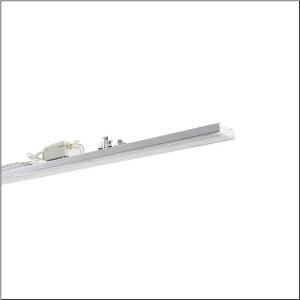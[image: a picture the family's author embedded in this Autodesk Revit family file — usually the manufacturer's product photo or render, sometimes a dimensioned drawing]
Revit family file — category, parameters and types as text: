
# Revit family: licross_r__11_recessed_mo_51te19mn495g_12e7
name_source: partatom
category: Lighting Fixtures
units: mm (PartAtom-declared; Revit-internal decimal feet)

## family parameters
Cut with Voids When Loaded = No
Host = Face
Light Source = No
Part Type = Normal
Room Calculation Point = No
Round Connector Dimension = Use Diameter
Shared = No

## types (1)
- --- (1 x LED, 9850 lm, 55.2 W, 4000K)
    Apparent Load = 55 VA
    CIE Flux Codes = 55 90 98 100 100
    Color Rendering = 80
    Color Temperature = 4000K
    Default Elevation = 1800 mm
    Description = Licross® 11 Recessed MO, luminaire insert, of sheet steel, galvanised, coil coated, white, length: 1.500mm, width: 66mm, height: 67mm, LED rated luminous flux: 9.860lm, light colour: 840, control gear: ON/OFF Multilumen, with plug, 3-pole, with phase selection, mains connection: 220..240V, AC, 50/60Hz, rated input power: 55W, halogen-free wiring, primary light control with lens, of plastic, primary optical cover: cover, of PMMA, light emission: direct distribution, primary light characteristic: double asymmetric, protection rating (complete): IP54, insulation class (complete): insulation class I (protective earthing), certification: CE, ENEC, VDE, UKCA, protection symbol: D if used in an environment with non-conductive dust loads with corresponding accessories, impact resistance: IK06, permissible ambient temperature for indoor applications: -35..+40°C, corresponds to IFS (International Featured Standards) requirements for safety and quality in the food industry, reducing of maximum allowable ambient temperature of 5°C with ceiling mounting, packaging unit: 1 piece
    Height = 58 mm
    Lamp = 1 x LED
    Lamp Light Flux = 9850 lm
    Lamp Power = 55.2 W
    Lamp count = 1
    Length = 1500 mm
    Luminous efficacy = 178 lm/W
    Manufacturer = Siteco
    ModVariant = No
    Model = 51TE19MN495G
    Mounting Place = Ceiling
    Mounting Type = Pendant
    Number of Poles = 1
    OnlyDefault = Yes
    Power Factor = 1
    Product Name = Licross® 11 Recessed MO
    Product group = luminaire insert
    ProductGroupID = 901
    Protection Class = Protection class I
    Protection Degree = IP 54
    RLX_Detail_Level = 1
    RLX_Emergency_Light_Flux = 0 lm
    RLX_Emergency_Type = 0
    RLX_Emergency_Type_DB = No
    RlxData = <blob elided: 22237 chars, md5=15443e5d>
    Socket = socket
    Standby Power = 0 W
    System Light Flux = 9850 lm
    System Power = 55 W
    Type Comments = factory setting: luminous flux: 100 % | (A | C | E) | 126 mA
    Type Image = l_1296930.jpg
    URL = http://relux.com
    VarID = @adj_055005
    Voltage = 0 V
    Weight = 0.00 kg
    Width = 66 mm

## geometry (parser evidence)
native form markers: Blend x4, Sweep x11
no freeform markers — native parametric forms only
